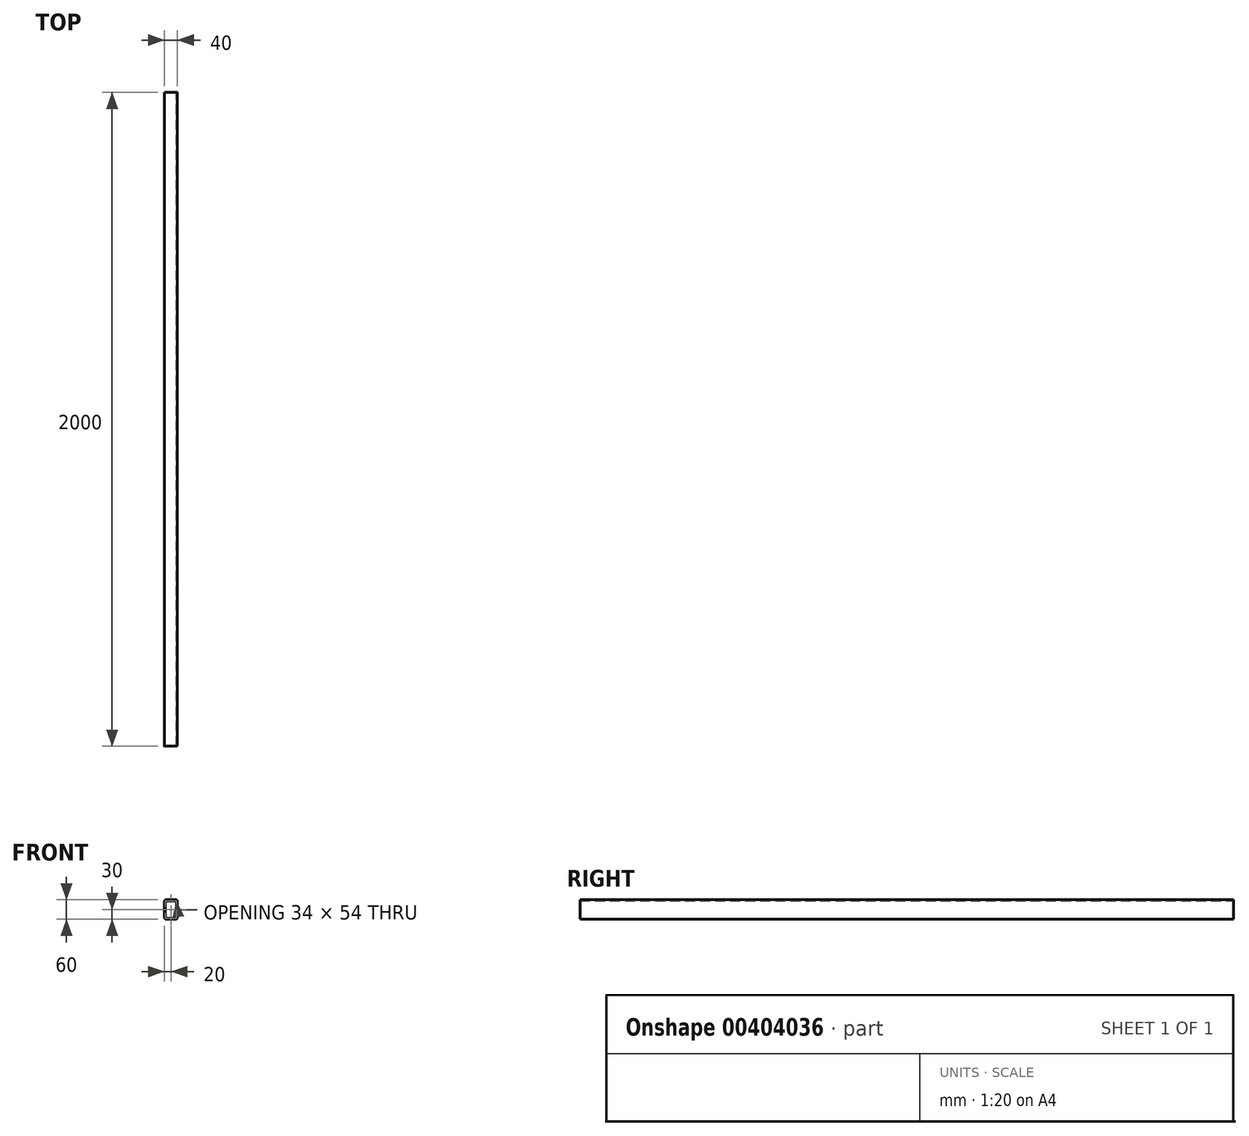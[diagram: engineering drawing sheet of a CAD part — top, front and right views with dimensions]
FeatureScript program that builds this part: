
annotation { "Feature Type Name" : "Feature", "Feature Type Description" : "" }
export const myFeature = defineFeature(function(context is Context, id is Id, definition is map)
    precondition{}
    {
        {
            var Q0;
            Q0=qCreatedBy(makeId("Front.planeOp"),FACE);
            var sketch = newSketch(context, id + "F0", { "sketchPlane" : qUnion([Q0])});
            skLineSegment(sketch, "E0.bottom", {"start": v(-14, 30) * mm, "end": v(14, 30) * mm});
            skLineSegment(sketch, "E0.top", {"start": v(-14, -30) * mm, "end": v(14, -30) * mm});
            skLineSegment(sketch, "E0.left", {"start": v(-20, 24) * mm, "end": v(-20, -24) * mm});
            skLineSegment(sketch, "E0.right", {"start": v(20, 24) * mm, "end": v(20, -24) * mm});
            skPoint(sketch, "E1.visualSharp", {"position": v(-20, 30) * mm});
            skArc(sketch, "E1.filletArc", {"start": v(-14, 30) * mm, "mid": v(-18.24, 28.24) * mm, "end": v(-20, 24) * mm});
            skPoint(sketch, "E2.visualSharp", {"position": v(-20, -30) * mm});
            skArc(sketch, "E2.filletArc", {"start": v(-20, -24) * mm, "mid": v(-18.24, -28.24) * mm, "end": v(-14, -30) * mm});
            skPoint(sketch, "E3.visualSharp", {"position": v(20, -30) * mm});
            skArc(sketch, "E3.filletArc", {"start": v(14, -30) * mm, "mid": v(18.24, -28.24) * mm, "end": v(20, -24) * mm});
            skPoint(sketch, "E4.visualSharp", {"position": v(20, 30) * mm});
            skArc(sketch, "E4.filletArc", {"start": v(20, 24) * mm, "mid": v(18.24, 28.24) * mm, "end": v(14, 30) * mm});
            skLineSegment(sketch, "E5.0", {"start": v(-17, 24) * mm, "end": v(-17, -24) * mm});
            skLineSegment(sketch, "E6.0", {"start": v(-14, 27) * mm, "end": v(14, 27) * mm});
            skArc(sketch, "E6.1", {"start": v(17, 24) * mm, "mid": v(16.12, 26.12) * mm, "end": v(14, 27) * mm});
            skLineSegment(sketch, "E6.2", {"start": v(17, 24) * mm, "end": v(17, -24) * mm});
            skArc(sketch, "E6.4", {"start": v(-17, -24) * mm, "mid": v(-16.12, -26.12) * mm, "end": v(-14, -27) * mm});
            skLineSegment(sketch, "E6.5", {"start": v(-14, -27) * mm, "end": v(14, -27) * mm});
            skArc(sketch, "E6.6", {"start": v(14, -27) * mm, "mid": v(16.12, -26.12) * mm, "end": v(17, -24) * mm});
            skArc(sketch, "E7.0", {"start": v(-14, 27) * mm, "mid": v(-16.12, 26.12) * mm, "end": v(-17, 24) * mm});
            skSolve(sketch);
        }
        {
            var Q0;
            Q0=makeQuery(id+"F0.imprint","IMPRINT",FACE,{"disambiguationData":[TD([[makeQuery(id+"F0.imprint","IMPRINT",EDGE,{"derivedFrom":sQuery(id+"F0.wireOp",EDGE,"E0.bottom")}),-1.0]])]});
            extrude(context, id + "F1", {"entities" : qUnion([Q0]), "depth" : 2000 * mm});
        }
    });
